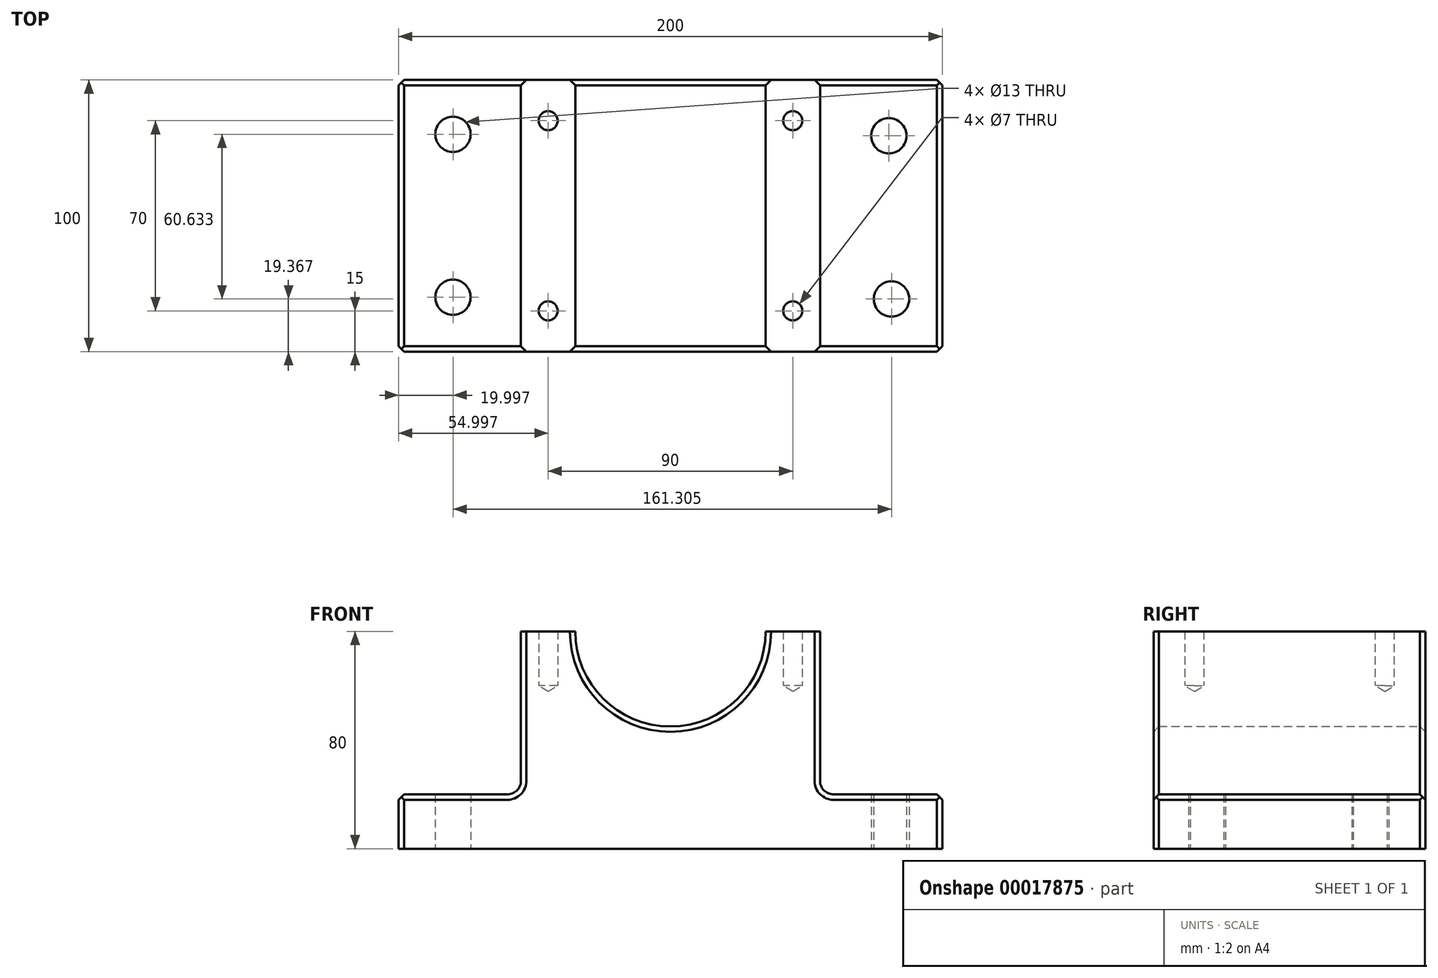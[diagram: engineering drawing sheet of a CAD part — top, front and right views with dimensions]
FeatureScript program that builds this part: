
annotation { "Feature Type Name" : "Feature", "Feature Type Description" : "" }
export const myFeature = defineFeature(function(context is Context, id is Id, definition is map)
    precondition{}
    {
        {
            var Q0;
            Q0=qCreatedBy(makeId("Front.planeOp"),FACE);
            var sketch = newSketch(context, id + "F0", { "sketchPlane" : qUnion([Q0])});
            skLineSegment(sketch, "E0", {"start": v(-722.13, 241.62) * mm, "end": v(-722.13, 221.62) * mm});
            skLineSegment(sketch, "E1", {"start": v(-722.13, 221.62) * mm, "end": v(-522.13, 221.62) * mm});
            skLineSegment(sketch, "E2", {"start": v(-522.13, 221.62) * mm, "end": v(-522.13, 241.62) * mm});
            skLineSegment(sketch, "E3", {"start": v(-522.13, 241.62) * mm, "end": v(-567.13, 241.62) * mm});
            skLineSegment(sketch, "E4", {"start": v(-567.13, 241.62) * mm, "end": v(-567.13, 301.62) * mm});
            skLineSegment(sketch, "E5", {"start": v(-567.13, 301.62) * mm, "end": v(-587.13, 301.62) * mm});
            skLineSegment(sketch, "E6", {"start": v(-722.13, 241.62) * mm, "end": v(-677.13, 241.62) * mm});
            skLineSegment(sketch, "E7", {"start": v(-677.13, 241.62) * mm, "end": v(-677.13, 301.62) * mm});
            skLineSegment(sketch, "E8", {"start": v(-677.13, 301.62) * mm, "end": v(-657.13, 301.62) * mm});
            skArc(sketch, "E9", {"start": v(-657.13, 301.62) * mm, "mid": v(-622.13, 266.62) * mm, "end": v(-587.13, 301.62) * mm});
            skSolve(sketch);
        }
        {
            var Q0;
            Q0=makeQuery(id+"F0.imprint","IMPRINT",FACE,{"disambiguationData":[TD([[makeQuery(id+"F0.imprint","IMPRINT",EDGE,{"derivedFrom":sQuery(id+"F0.wireOp",EDGE,"E0")}),1.0]])]});
            extrude(context, id + "F1", {"entities" : qUnion([Q0]), "depth" : 100 * mm});
        }
        {
            var Q0;
            Q0=makeQuery(id+"F1.opExtrude","SWEPT_FACE",FACE,{"disambiguationData":[OSD([sQuery(id+"F0.wireOp",EDGE,"E6")])]});
            var sketch = newSketch(context, id + "F2", { "sketchPlane" : qUnion([Q0])});
            skLineSegment(sketch, "E10", {"start": v(-702.13, 9.25) * mm, "end": v(-702.13, -117.66) * mm});
            skLineSegment(sketch, "E11", {"start": v(-702.13, -80) * mm, "end": v(-751.28, -80) * mm});
            skLineSegment(sketch, "E12", {"start": v(-702.13, -20) * mm, "end": v(-745.92, -20) * mm});
            skSolve(sketch);
        }
        {
            var Q0;
            Q0=sQuery(id+"F2.wireOp",VERTEX,"E11.start");
            var Q1;
            Q1=sQuery(id+"F2.wireOp",VERTEX,"E12.start");
            var Q2;
            Q2=makeQuery(id+"F1.opExtrude","SWEPT_BODY",BODY,{"disambiguationData":[OSD([sQuery(id+"F0.wireOp",EDGE,"E0"),sQuery(id+"F0.wireOp",EDGE,"E1"),sQuery(id+"F0.wireOp",EDGE,"E2"),sQuery(id+"F0.wireOp",EDGE,"E3"),sQuery(id+"F0.wireOp",EDGE,"E4"),sQuery(id+"F0.wireOp",EDGE,"E5"),sQuery(id+"F0.wireOp",EDGE,"E6"),sQuery(id+"F0.wireOp",EDGE,"E7"),sQuery(id+"F0.wireOp",EDGE,"E8"),sQuery(id+"F0.wireOp",EDGE,"E9")])]});
            hole(context, id + "F3", {"style" : HoleStyle.SIMPLE, "holeDiameter" : 13 * mm, "endStyle" : HoleEndStyle.THROUGH, "locations" : qUnion([Q0, Q1]), "scope" : qUnion([Q2])});
        }
        {
            var Q0;
            Q0=makeQuery(id+"F1.opExtrude","SWEPT_FACE",FACE,{"disambiguationData":[OSD([sQuery(id+"F0.wireOp",EDGE,"E3")])]});
            var sketch = newSketch(context, id + "F4", { "sketchPlane" : qUnion([Q0])});
            skLineSegment(sketch, "E13", {"start": v(-542.35, 13.05) * mm, "end": v(-540.08, -126.49) * mm});
            skLineSegment(sketch, "E14", {"start": v(-541.8, -20.55) * mm, "end": v(-507.62, -20) * mm});
            skLineSegment(sketch, "E15", {"start": v(-540.83, -80.63) * mm, "end": v(-501.78, -80) * mm});
            skSolve(sketch);
        }
        {
            var Q0;
            Q0=sQuery(id+"F4.wireOp",VERTEX,"E14.start");
            var Q1;
            Q1=sQuery(id+"F4.wireOp",VERTEX,"E15.start");
            var Q2;
            Q2=makeQuery(id+"F1.opExtrude","SWEPT_BODY",BODY,{"disambiguationData":[OSD([sQuery(id+"F0.wireOp",EDGE,"E0"),sQuery(id+"F0.wireOp",EDGE,"E1"),sQuery(id+"F0.wireOp",EDGE,"E2"),sQuery(id+"F0.wireOp",EDGE,"E3"),sQuery(id+"F0.wireOp",EDGE,"E4"),sQuery(id+"F0.wireOp",EDGE,"E5"),sQuery(id+"F0.wireOp",EDGE,"E6"),sQuery(id+"F0.wireOp",EDGE,"E7"),sQuery(id+"F0.wireOp",EDGE,"E8"),sQuery(id+"F0.wireOp",EDGE,"E9")])]});
            hole(context, id + "F5", {"style" : HoleStyle.SIMPLE, "holeDiameter" : 13 * mm, "endStyle" : HoleEndStyle.THROUGH, "locations" : qUnion([Q0, Q1]), "scope" : qUnion([Q2])});
        }
        {
            var Q0;
            Q0=makeQuery(id+"F1.opExtrude","SWEPT_FACE",FACE,{"disambiguationData":[OSD([sQuery(id+"F0.wireOp",EDGE,"E8")])]});
            var sketch = newSketch(context, id + "F6", { "sketchPlane" : qUnion([Q0])});
            skLineSegment(sketch, "E16", {"start": v(-667.13, 0) * mm, "end": v(-667.13, -100) * mm});
            skLineSegment(sketch, "E17", {"start": v(-667.13, -15) * mm, "end": v(-695.14, -15) * mm});
            skLineSegment(sketch, "E18", {"start": v(-667.13, -85) * mm, "end": v(-694.44, -85) * mm});
            skSolve(sketch);
        }
        {
            var Q0;
            Q0=sQuery(id+"F6.wireOp",VERTEX,"E17.start");
            var Q1;
            Q1=sQuery(id+"F6.wireOp",VERTEX,"E18.start");
            var Q2;
            Q2=makeQuery(id+"F1.opExtrude","SWEPT_BODY",BODY,{"disambiguationData":[OSD([sQuery(id+"F0.wireOp",EDGE,"E0"),sQuery(id+"F0.wireOp",EDGE,"E1"),sQuery(id+"F0.wireOp",EDGE,"E2"),sQuery(id+"F0.wireOp",EDGE,"E3"),sQuery(id+"F0.wireOp",EDGE,"E4"),sQuery(id+"F0.wireOp",EDGE,"E5"),sQuery(id+"F0.wireOp",EDGE,"E6"),sQuery(id+"F0.wireOp",EDGE,"E7"),sQuery(id+"F0.wireOp",EDGE,"E8"),sQuery(id+"F0.wireOp",EDGE,"E9")])]});
            hole(context, id + "F7", {"style" : HoleStyle.SIMPLE, "holeDiameter" : 7 * mm, "endStyle" : HoleEndStyle.BLIND, "holeDepth" : 20 * mm, "locations" : qUnion([Q0, Q1]), "scope" : qUnion([Q2])});
        }
        {
            var Q0;
            Q0=makeQuery(id+"F1.opExtrude","SWEPT_FACE",FACE,{"disambiguationData":[OSD([sQuery(id+"F0.wireOp",EDGE,"E5")])]});
            var sketch = newSketch(context, id + "F8", { "sketchPlane" : qUnion([Q0])});
            skLineSegment(sketch, "E19", {"start": v(-577.13, 0) * mm, "end": v(-577.13, -100) * mm});
            skLineSegment(sketch, "E20", {"start": v(-577.13, -15) * mm, "end": v(-550.38, -15) * mm});
            skLineSegment(sketch, "E21", {"start": v(-577.13, -85) * mm, "end": v(-547.68, -85) * mm});
            skSolve(sketch);
        }
        {
            var Q0;
            Q0=sQuery(id+"F8.wireOp",VERTEX,"E20.start");
            var Q1;
            Q1=sQuery(id+"F8.wireOp",VERTEX,"E21.start");
            var Q2;
            Q2=makeQuery(id+"F1.opExtrude","SWEPT_BODY",BODY,{"disambiguationData":[OSD([sQuery(id+"F0.wireOp",EDGE,"E0"),sQuery(id+"F0.wireOp",EDGE,"E1"),sQuery(id+"F0.wireOp",EDGE,"E2"),sQuery(id+"F0.wireOp",EDGE,"E3"),sQuery(id+"F0.wireOp",EDGE,"E4"),sQuery(id+"F0.wireOp",EDGE,"E5"),sQuery(id+"F0.wireOp",EDGE,"E6"),sQuery(id+"F0.wireOp",EDGE,"E7"),sQuery(id+"F0.wireOp",EDGE,"E8"),sQuery(id+"F0.wireOp",EDGE,"E9")])]});
            hole(context, id + "F9", {"style" : HoleStyle.SIMPLE, "holeDiameter" : 7 * mm, "endStyle" : HoleEndStyle.BLIND, "holeDepth" : 20 * mm, "locations" : qUnion([Q0, Q1]), "scope" : qUnion([Q2])});
        }
        {
            var Q0;
            Q0=makeQuery(id+"F1.opExtrude","SWEPT_EDGE",EDGE,{"disambiguationData":[OSD([sQuery(id+"F0.wireOp",EDGE,"E6"),sQuery(id+"F0.wireOp",EDGE,"E7")])]});
            var Q1;
            Q1=makeQuery(id+"F1.opExtrude","SWEPT_EDGE",EDGE,{"disambiguationData":[OSD([sQuery(id+"F0.wireOp",EDGE,"E3"),sQuery(id+"F0.wireOp",EDGE,"E4")])]});
            fillet(context, id + "F10", {"entities" : qUnion([Q0, Q1]), "radius" : 5 * mm, "tangentPropagation" : true, "allowEdgeOverflow" : false});
        }
        {
            var Q0;
            Q0=makeQuery(id+"F1.opExtrude","SWEPT_EDGE",EDGE,{"disambiguationData":[OSD([sQuery(id+"F0.wireOp",EDGE,"E2"),sQuery(id+"F0.wireOp",EDGE,"E3")])]});
            chamfer(context, id + "F11", {"entities" : qUnion([Q0]), "width" : 2 * mm, "tangentPropagation" : true});
        }
        {
            var Q0;
            Q0=makeQuery(id+"F1.opExtrude","SWEPT_EDGE",EDGE,{"disambiguationData":[OSD([sQuery(id+"F0.wireOp",EDGE,"E0"),sQuery(id+"F0.wireOp",EDGE,"E6")])]});
            chamfer(context, id + "F12", {"entities" : qUnion([Q0]), "width" : 2 * mm, "tangentPropagation" : true});
        }
        {
            var Q0;
            Q0=makeQuery(id+"F1.opExtrude","CAP_EDGE",EDGE,{"disambiguationData":[OSD([sQuery(id+"F0.wireOp",EDGE,"E9")])],"isStart":true});
            var Q1;
            Q1=makeQuery(id+"F1.opExtrude","CAP_EDGE",EDGE,{"disambiguationData":[OSD([sQuery(id+"F0.wireOp",EDGE,"E4")])],"isStart":true});
            var Q2;
            Q2=makeQuery(id+"F1.opExtrude","CAP_EDGE",EDGE,{"disambiguationData":[OSD([sQuery(id+"F0.wireOp",EDGE,"E3")])],"isStart":true});
            var Q3;
            Q3=makeQuery(id+"F1.opExtrude","CAP_EDGE",EDGE,{"disambiguationData":[OSD([sQuery(id+"F0.wireOp",EDGE,"E2")])],"isStart":true});
            var Q4;
            Q4=makeQuery(id+"F1.opExtrude","CAP_EDGE",EDGE,{"disambiguationData":[OSD([sQuery(id+"F0.wireOp",EDGE,"E7")])],"isStart":true});
            var Q5;
            Q5=makeQuery(id+"F1.opExtrude","CAP_EDGE",EDGE,{"disambiguationData":[OSD([sQuery(id+"F0.wireOp",EDGE,"E0")])],"isStart":true});
            var Q6;
            Q6=makeQuery(id+"F1.opExtrude","CAP_EDGE",EDGE,{"disambiguationData":[OSD([sQuery(id+"F0.wireOp",EDGE,"E2")])],"isStart":false});
            var Q7;
            Q7=makeQuery(id+"F1.opExtrude","CAP_EDGE",EDGE,{"disambiguationData":[OSD([sQuery(id+"F0.wireOp",EDGE,"E3")])],"isStart":false});
            var Q8;
            Q8=makeQuery(id+"F1.opExtrude","CAP_EDGE",EDGE,{"disambiguationData":[OSD([sQuery(id+"F0.wireOp",EDGE,"E4")])],"isStart":false});
            var Q9;
            Q9=makeQuery(id+"F1.opExtrude","CAP_EDGE",EDGE,{"disambiguationData":[OSD([sQuery(id+"F0.wireOp",EDGE,"E7")])],"isStart":false});
            var Q10;
            Q10=makeQuery(id+"F1.opExtrude","CAP_EDGE",EDGE,{"disambiguationData":[OSD([sQuery(id+"F0.wireOp",EDGE,"E6")])],"isStart":false});
            var Q11;
            Q11=makeQuery(id+"F1.opExtrude","CAP_EDGE",EDGE,{"disambiguationData":[OSD([sQuery(id+"F0.wireOp",EDGE,"E0")])],"isStart":false});
            chamfer(context, id + "F13", {"entities" : qUnion([Q0, Q1, Q2, Q3, Q4, Q5, Q6, Q7, Q8, Q9, Q10, Q11]), "width" : 2 * mm, "tangentPropagation" : true});
        }
        {
            var Q0;
            Q0=makeQuery(id+"F1.opExtrude","CAP_EDGE",EDGE,{"disambiguationData":[OSD([sQuery(id+"F0.wireOp",EDGE,"E9")])],"isStart":false});
            chamfer(context, id + "F14", {"entities" : qUnion([Q0]), "width" : 2 * mm, "tangentPropagation" : true});
        }
    });
